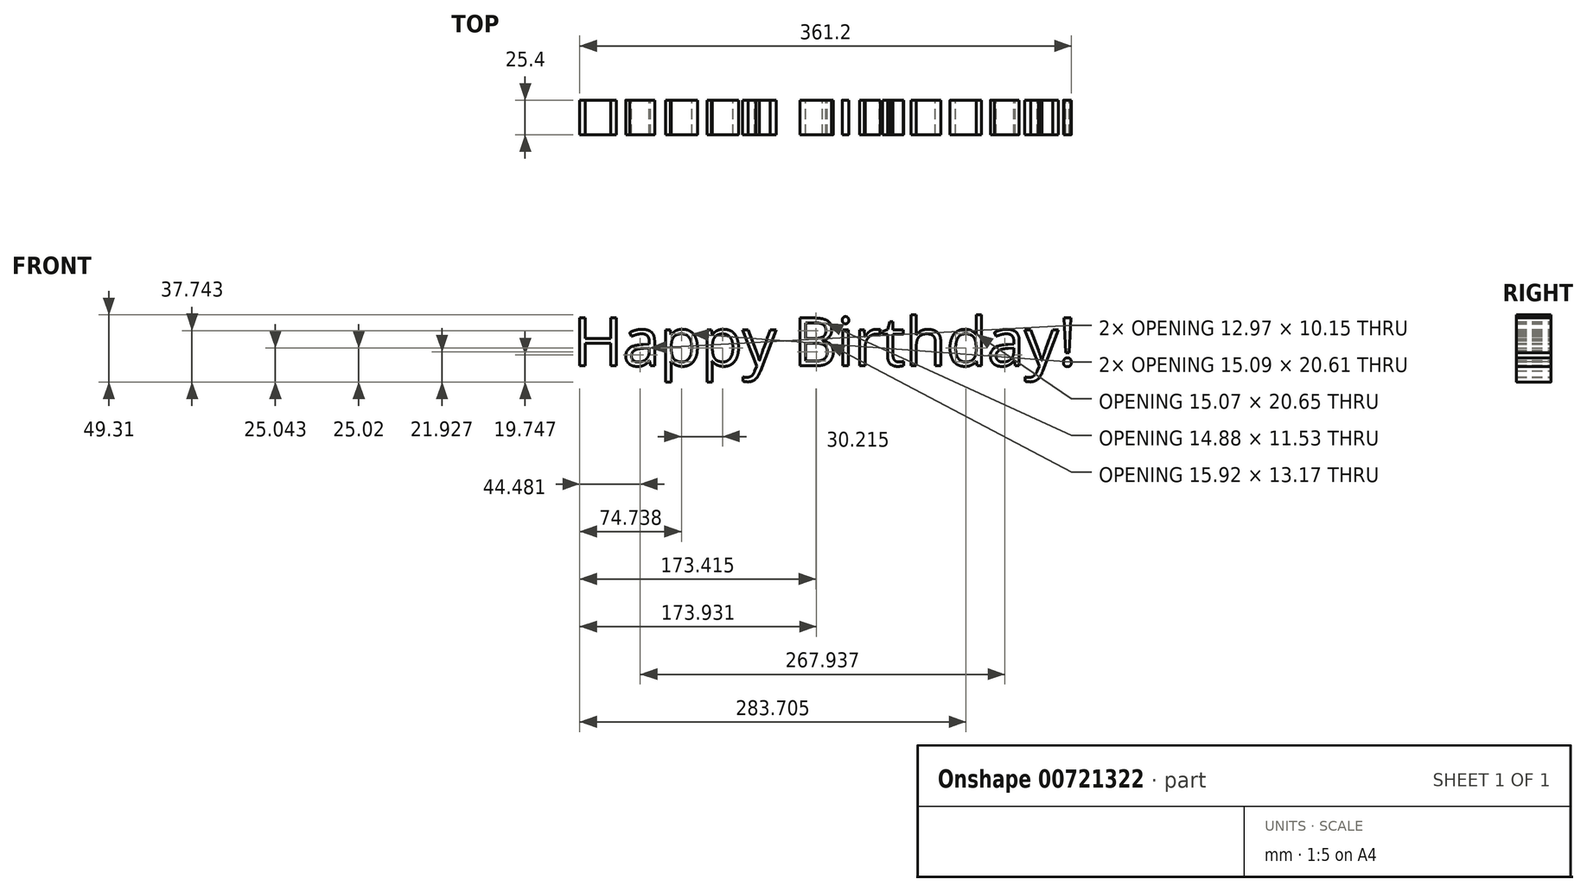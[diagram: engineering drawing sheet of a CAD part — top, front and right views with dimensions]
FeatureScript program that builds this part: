
annotation { "Feature Type Name" : "Feature", "Feature Type Description" : "" }
export const myFeature = defineFeature(function(context is Context, id is Id, definition is map)
    precondition{}
    {
        {
            var Q0;
            Q0=qCreatedBy(makeId("Front.planeOp"),FACE);
            var sketch = newSketch(context, id + "F0", { "sketchPlane" : qUnion([Q0])});
            skText(sketch, "E0", { "text": "Happy Birthday!", "fontName": "OpenSans-Regular.ttf"});
            const initialGuessF0  = {"E0": [-0.03035, -0.00374, 1, 0, 0.0355]};
            skSetInitialGuess(sketch, initialGuessF0);
            skSolve(sketch);
        }
        {
            var Q0;
            Q0 = qSketchRegion(id + "F0", true);
            extrude(context, id + "F1", {"entities" : qUnion([Q0]), "depth" : 25.4 * mm, "offsetDistance" : 25.4 * mm});
        }
    });
